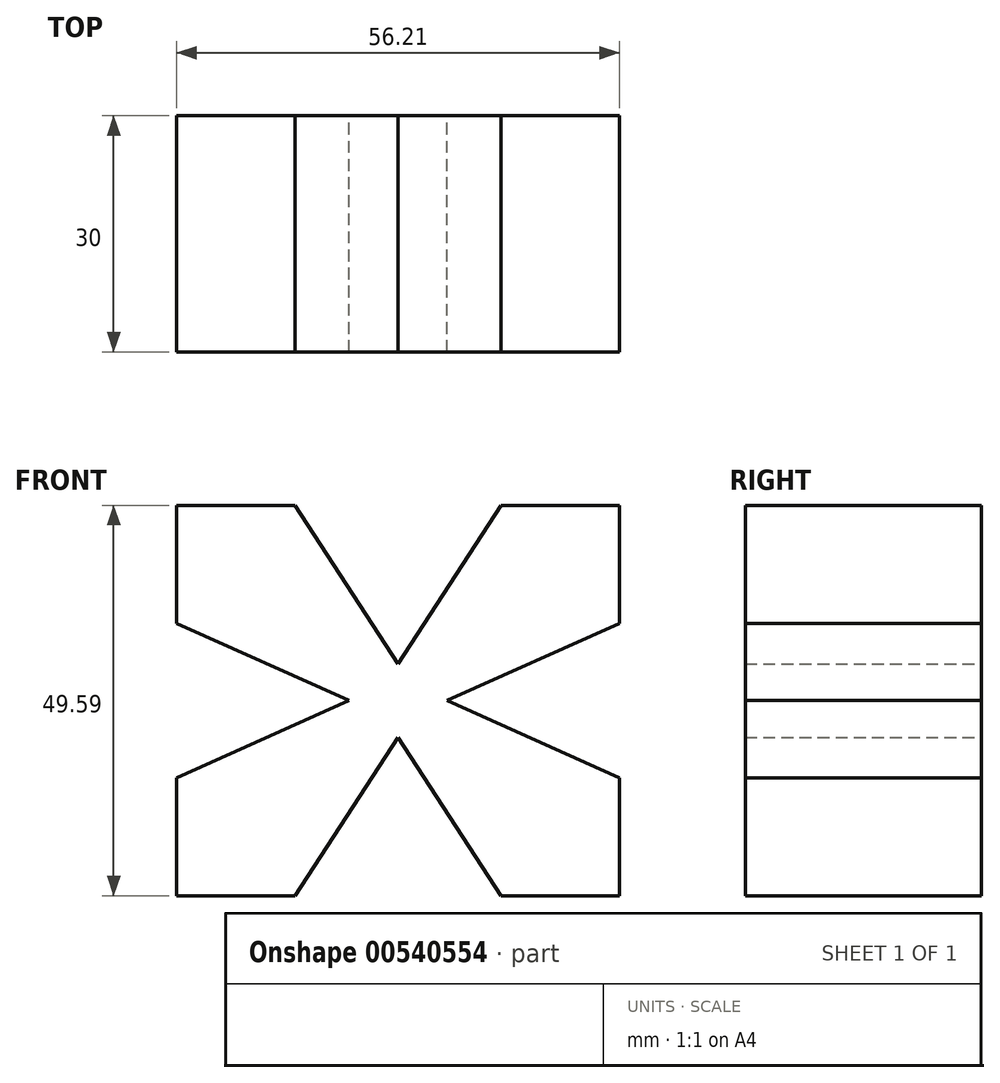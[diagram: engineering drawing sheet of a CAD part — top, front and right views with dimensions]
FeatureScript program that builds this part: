
annotation { "Feature Type Name" : "Feature", "Feature Type Description" : "" }
export const myFeature = defineFeature(function(context is Context, id is Id, definition is map)
    precondition{}
    {
        {
            var Q0;
            Q0=qCreatedBy(makeId("Front.planeOp"),FACE);
            var sketch = newSketch(context, id + "F0", { "sketchPlane" : qUnion([Q0])});
            skLineSegment(sketch, "E0", {"start": v(-41.21, -17) * mm, "end": v(-26.21, -17) * mm});
            skLineSegment(sketch, "E1", {"start": v(-26.21, -17) * mm, "end": v(-13.1, 3.1) * mm});
            skLineSegment(sketch, "E2", {"start": v(-13.1, 3.1) * mm, "end": v(0, -17) * mm});
            skLineSegment(sketch, "E3", {"start": v(0, -17) * mm, "end": v(15, -17) * mm});
            skLineSegment(sketch, "E4", {"start": v(15, -17) * mm, "end": v(15, -2) * mm});
            skLineSegment(sketch, "E5", {"start": v(15, -2) * mm, "end": v(-6.91, 7.8) * mm});
            skLineSegment(sketch, "E6", {"start": v(-6.91, 7.8) * mm, "end": v(15, 17.59) * mm});
            skLineSegment(sketch, "E7", {"start": v(15, 17.59) * mm, "end": v(15, 32.59) * mm});
            skLineSegment(sketch, "E8", {"start": v(15, 32.59) * mm, "end": v(0, 32.59) * mm});
            skLineSegment(sketch, "E9", {"start": v(0, 32.59) * mm, "end": v(-13.1, 12.48) * mm});
            skLineSegment(sketch, "E10", {"start": v(-13.1, 12.48) * mm, "end": v(-26.21, 32.59) * mm});
            skLineSegment(sketch, "E11", {"start": v(-26.21, 32.59) * mm, "end": v(-41.21, 32.59) * mm});
            skLineSegment(sketch, "E12", {"start": v(-41.21, 32.59) * mm, "end": v(-41.21, 17.59) * mm});
            skLineSegment(sketch, "E13", {"start": v(-41.21, 17.59) * mm, "end": v(-19.3, 7.8) * mm});
            skLineSegment(sketch, "E14", {"start": v(-19.3, 7.8) * mm, "end": v(-41.21, -2) * mm});
            skLineSegment(sketch, "E15", {"start": v(-41.21, -2) * mm, "end": v(-41.21, -17) * mm});
            skSolve(sketch);
        }
        {
            var Q0;
            Q0 = qSketchRegion(id + "F0", true);
            extrude(context, id + "F1", {"entities" : qUnion([Q0]), "depth" : 30 * mm, "offsetDistance" : 25 * mm});
        }
    });
